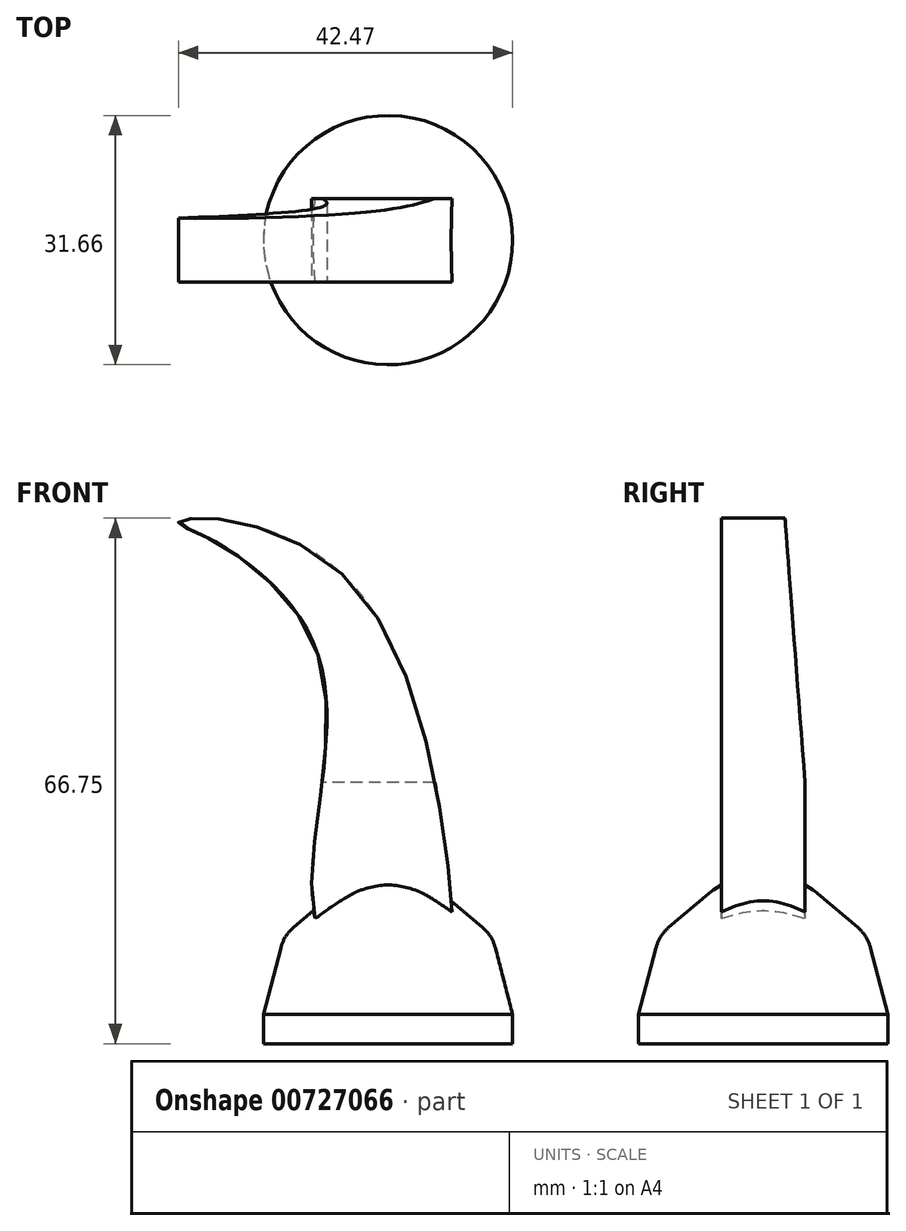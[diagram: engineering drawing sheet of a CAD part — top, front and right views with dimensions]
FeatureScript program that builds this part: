
annotation { "Feature Type Name" : "Feature", "Feature Type Description" : "" }
export const myFeature = defineFeature(function(context is Context, id is Id, definition is map)
    precondition{}
    {
        {
            var Q0;
            Q0=qCreatedBy(makeId("Front.planeOp"),FACE);
            var sketch = newSketch(context, id + "F0", { "sketchPlane" : qUnion([Q0])});
            skLineSegment(sketch, "E0", {"start": v(0, 0) * mm, "end": v(-15.83, 0) * mm});
            skLineSegment(sketch, "E1", {"start": v(-15.83, 0) * mm, "end": v(-15.83, 3.7) * mm});
            skLineSegment(sketch, "E2", {"start": v(-15.83, 3.7) * mm, "end": v(-13.23, 13.73) * mm});
            skLineSegment(sketch, "E3", {"start": v(-13.23, 13.73) * mm, "end": v(-6.61, 19.34) * mm});
            skLineSegment(sketch, "E4", {"start": v(-6.61, 19.34) * mm, "end": v(-2.4, 21.94) * mm});
            skLineSegment(sketch, "E5", {"start": v(-2.4, 21.94) * mm, "end": v(0, 21.94) * mm});
            skLineSegment(sketch, "E6", {"start": v(0, 21.94) * mm, "end": v(0, 0) * mm});
            skSolve(sketch);
        }
        {
            var Q0;
            Q0 = qSketchRegion(id + "F0", true);
            var Q1;
            Q1=sQuery(id+"F0.wireOp",EDGE,"E6");
            revolve(context, id + "F1", {"surfaceOperationType" : NewSurfaceOperationType.NEW, "entities" : qUnion([Q0]), "axis" : qUnion([Q1]), "revolveType" : RevolveType.FULL});
        }
        {
            var Q0;
            Q0=makeQuery(id+"F1.opRevolve","SWEPT_FACE",FACE,{"disambiguationData":[OSD([sQuery(id+"F0.wireOp",EDGE,"E4")])]});
            fillet(context, id + "F2", {"entities" : qUnion([Q0]), "radius" : 5 * mm, "tangentPropagation" : true, "allowEdgeOverflow" : false});
        }
        {
            var Q0;
            Q0=makeQuery(id+"F1.opRevolve","SWEPT_FACE",FACE,{"disambiguationData":[OSD([sQuery(id+"F0.wireOp",EDGE,"E3")])]});
            fillet(context, id + "F3", {"entities" : qUnion([Q0]), "radius" : 5 * mm, "tangentPropagation" : true, "allowEdgeOverflow" : false});
        }
        {
            var Q0;
            Q0=qCreatedBy(makeId("Front.planeOp"),FACE);
            var sketch = newSketch(context, id + "F4", { "sketchPlane" : qUnion([Q0])});
            skFitSpline(sketch, "E7", {"points": [v(-24.23, 66.74) * mm, v(-3, 56.52) * mm, v(8.23, 14.84) * mm, v(7.03, 11.64) * mm, v(-5.8, 11.24) * mm, v(-9.6, 23.06) * mm, v(-9.2, 50.31) * mm, v(-23.43, 64.54) * mm, v(-26.64, 66.14) * mm, v(-24.23, 66.74) * mm]});
            skSolve(sketch);
        }
        {
            var Q0;
            Q0=makeQuery(id+"F4.imprint","IMPRINT",FACE,{"disambiguationData":[TD([[makeQuery(id+"F4.imprint","IMPRINT",EDGE,{"derivedFrom":sQuery(id+"F4.wireOp",EDGE,"E7")}),-1.0]])]});
            extrude(context, id + "F5", {"entities" : qUnion([Q0]), "operationType" : NewBodyOperationType.ADD, "endBound" : BoundingType.SYMMETRIC, "depth" : 10.6 * mm, "offsetDistance" : 25 * mm});
        }
        {
            var Q0;
            Q0=qCreatedBy(makeId("Right.planeOp"),FACE);
            var sketch = newSketch(context, id + "F6", { "sketchPlane" : qUnion([Q0])});
            skLineSegment(sketch, "E8", {"start": v(2.6, 68.83) * mm, "end": v(6.21, 21.14) * mm});
            skLineSegment(sketch, "E9", {"start": v(6.21, 21.14) * mm, "end": v(14.43, 70.43) * mm});
            skLineSegment(sketch, "E10", {"start": v(14.43, 70.43) * mm, "end": v(2.6, 68.83) * mm});
            skSolve(sketch);
        }
        {
            var Q0;
            Q0=makeQuery(id+"F6.imprint","IMPRINT",FACE,{"disambiguationData":[TD([[makeQuery(id+"F6.imprint","IMPRINT",EDGE,{"derivedFrom":sQuery(id+"F6.wireOp",EDGE,"E8")}),1.0]])]});
            extrude(context, id + "F7", {"entities" : qUnion([Q0]), "operationType" : NewBodyOperationType.REMOVE, "endBound" : BoundingType.SYMMETRIC, "depth" : 58.6 * mm, "offsetDistance" : 25 * mm});
        }
    });
